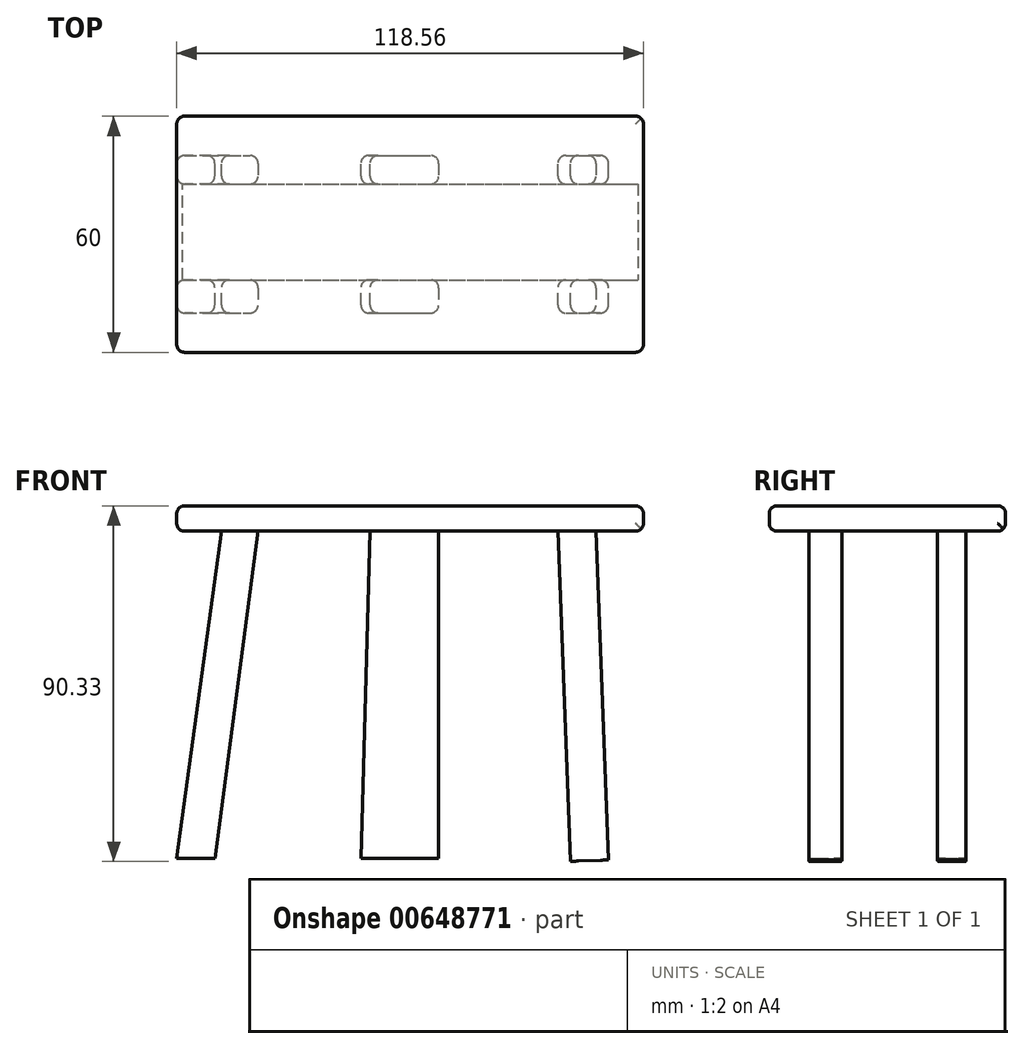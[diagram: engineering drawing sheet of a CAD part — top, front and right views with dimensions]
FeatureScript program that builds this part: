
annotation { "Feature Type Name" : "Feature", "Feature Type Description" : "" }
export const myFeature = defineFeature(function(context is Context, id is Id, definition is map)
    precondition{}
    {
        {
            var Q0;
            Q0=qCreatedBy(makeId("Front.planeOp"),FACE);
            var sketch = newSketch(context, id + "F0", { "sketchPlane" : qUnion([Q0])});
            skLineSegment(sketch, "E0.bottom", {"start": v(-56.26, 27.02) * mm, "end": v(62.3, 27.02) * mm});
            skLineSegment(sketch, "E0.top", {"start": v(-56.26, 20.57) * mm, "end": v(62.3, 20.57) * mm});
            skLineSegment(sketch, "E0.left", {"start": v(-56.26, 27.02) * mm, "end": v(-56.26, 20.57) * mm});
            skLineSegment(sketch, "E0.right", {"start": v(62.3, 27.02) * mm, "end": v(62.3, 20.57) * mm});
            skSolve(sketch);
        }
        {
            var Q0;
            Q0=makeQuery(id+"F0.imprint","IMPRINT",FACE,{"disambiguationData":[TD([[makeQuery(id+"F0.imprint","IMPRINT",EDGE,{"derivedFrom":sQuery(id+"F0.wireOp",EDGE,"E0.bottom")}),-1.0]])]});
            extrude(context, id + "F1", {"entities" : qUnion([Q0]), "depth" : 60 * mm, "offsetDistance" : 25 * mm});
        }
        {
            var Q0;
            Q0=qCreatedBy(makeId("Front.planeOp"),FACE);
            cPlane(context, id + "F2", {"entities" : qUnion([Q0]), "cplaneType" : CPlaneType.OFFSET, "offset" : 10 * mm, "width" : 150 * mm, "height" : 150 * mm});
        }
        {
            var Q0;
            Q0=qCreatedBy(id+"F2.planeOp",FACE);
            var sketch = newSketch(context, id + "F3", { "sketchPlane" : qUnion([Q0])});
            skLineSegment(sketch, "E1", {"start": v(-44.56, 22.99) * mm, "end": v(-56.26, -62.5) * mm});
            skLineSegment(sketch, "E2", {"start": v(-56.26, -62.5) * mm, "end": v(-46.58, -62.5) * mm});
            skLineSegment(sketch, "E3", {"start": v(-46.58, -62.5) * mm, "end": v(-35.29, 22.99) * mm});
            skLineSegment(sketch, "E4", {"start": v(-35.29, 22.99) * mm, "end": v(-44.56, 22.99) * mm});
            skLineSegment(sketch, "E5", {"start": v(-7.06, 22.99) * mm, "end": v(-9.48, -62.5) * mm});
            skPoint(sketch, "E5.startSnap0", {"position": v(-39.92, 22.99) * mm});
            skLineSegment(sketch, "E6", {"start": v(-9.48, -62.5) * mm, "end": v(10.28, -62.5) * mm});
            skLineSegment(sketch, "E7", {"start": v(10.28, -62.5) * mm, "end": v(10.28, 22.99) * mm});
            skLineSegment(sketch, "E8", {"start": v(10.28, 22.99) * mm, "end": v(-7.06, 22.99) * mm});
            skLineSegment(sketch, "E9", {"start": v(40.53, 22.18) * mm, "end": v(43.75, -63.31) * mm});
            skLineSegment(sketch, "E10", {"start": v(43.75, -63.31) * mm, "end": v(53.42, -62.95) * mm});
            skLineSegment(sketch, "E11", {"start": v(53.42, -62.95) * mm, "end": v(50.2, 22.27) * mm});
            skLineSegment(sketch, "E12", {"start": v(50.2, 22.27) * mm, "end": v(40.53, 22.18) * mm});
            skSolve(sketch);
        }
        {
            var Q0;
            Q0 = qSketchRegion(id + "F3", true);
            extrude(context, id + "F4", {"entities" : qUnion([Q0]), "operationType" : NewBodyOperationType.ADD, "depth" : 40 * mm, "offsetDistance" : 25 * mm});
        }
        {
            var Q0;
            Q0=qCreatedBy(makeId("Right.planeOp"),FACE);
            var sketch = newSketch(context, id + "F5", { "sketchPlane" : qUnion([Q0])});
            skLineSegment(sketch, "E13.bottom", {"start": v(-41.6, 20.65) * mm, "end": v(-17.23, 20.65) * mm});
            skLineSegment(sketch, "E13.top", {"start": v(-41.6, -66.54) * mm, "end": v(-17.23, -66.54) * mm});
            skLineSegment(sketch, "E13.left", {"start": v(-41.6, 20.65) * mm, "end": v(-41.6, -66.54) * mm});
            skLineSegment(sketch, "E13.right", {"start": v(-17.23, 20.65) * mm, "end": v(-17.23, -66.54) * mm});
            skSolve(sketch);
        }
        {
            var Q0;
            Q0 = qSketchRegion(id + "F5", true);
            extrude(context, id + "F6", {"entities" : qUnion([Q0]), "operationType" : NewBodyOperationType.REMOVE, "endBound" : BoundingType.THROUGH_ALL, "oppositeDirection" : true, "depth" : 100 * mm, "offsetDistance" : 25 * mm, "hasSecondDirection" : true, "secondDirectionOppositeDirection" : false, "secondDirectionDepth" : 100 * mm});
        }
        {
            var Q0;
            Q0=makeQuery(id+"F1.opExtrude","SWEPT_EDGE",EDGE,{"disambiguationData":[OSD([sQuery(id+"F0.wireOp",EDGE,"E0.bottom"),sQuery(id+"F0.wireOp",EDGE,"E0.left")])]});
            var Q1;
            Q1=makeQuery(id+"F1.opExtrude","CAP_EDGE",EDGE,{"disambiguationData":[OSD([sQuery(id+"F0.wireOp",EDGE,"E0.bottom")])],"isStart":false});
            var Q2;
            Q2=makeQuery(id+"F1.opExtrude","SWEPT_EDGE",EDGE,{"disambiguationData":[OSD([sQuery(id+"F0.wireOp",EDGE,"E0.bottom"),sQuery(id+"F0.wireOp",EDGE,"E0.right")])]});
            var Q3;
            Q3=makeQuery(id+"F1.opExtrude","CAP_EDGE",EDGE,{"disambiguationData":[OSD([sQuery(id+"F0.wireOp",EDGE,"E0.bottom")])],"isStart":true});
            var Q4;
            Q4=makeQuery(id+"F1.opExtrude","CAP_EDGE",EDGE,{"disambiguationData":[OSD([sQuery(id+"F0.wireOp",EDGE,"E0.left")])],"isStart":false});
            var Q5;
            Q5=makeQuery(id+"F1.opExtrude","CAP_EDGE",EDGE,{"disambiguationData":[OSD([sQuery(id+"F0.wireOp",EDGE,"E0.left")])],"isStart":true});
            var Q6;
            {var subQ0=sQuery(id+"F0.wireOp",EDGE,"E0.left");var subQ1=sQuery(id+"F0.wireOp",EDGE,"E0.top");Q6=makeQuery(id+"F6.boolean.opBoolean","SPLIT",EDGE,{"disambiguationData":[TD([makeQuery(id+"F6.opExtrude","SWEPT_FACE",FACE,{"disambiguationData":[OSD([sQuery(id+"F5.wireOp",EDGE,"E13.right")])]})])],"derivedFrom":makeQuery(id+"F1.opExtrude","SWEPT_EDGE",EDGE,{"disambiguationData":[OSD([subQ1,subQ0])]})});}
            var Q7;
            {var subQ0=sQuery(id+"F0.wireOp",EDGE,"E0.left");var subQ1=sQuery(id+"F0.wireOp",EDGE,"E0.top");Q7=makeQuery(id+"F6.boolean.opBoolean","SPLIT",EDGE,{"disambiguationData":[TD([makeQuery(id+"F6.opExtrude","SWEPT_FACE",FACE,{"disambiguationData":[OSD([sQuery(id+"F5.wireOp",EDGE,"E13.left")])]})])],"derivedFrom":makeQuery(id+"F1.opExtrude","SWEPT_EDGE",EDGE,{"disambiguationData":[OSD([subQ1,subQ0])]})});}
            var Q8;
            {var subQ0=sQuery(id+"F0.wireOp",EDGE,"E0.right");var subQ1=sQuery(id+"F0.wireOp",EDGE,"E0.top");Q8=makeQuery(id+"F6.boolean.opBoolean","SPLIT",EDGE,{"disambiguationData":[TD([makeQuery(id+"F6.opExtrude","SWEPT_FACE",FACE,{"disambiguationData":[OSD([sQuery(id+"F5.wireOp",EDGE,"E13.left")])]})])],"derivedFrom":makeQuery(id+"F1.opExtrude","SWEPT_EDGE",EDGE,{"disambiguationData":[OSD([subQ1,subQ0])]})});}
            var Q9;
            Q9=makeQuery(id+"F1.opExtrude","CAP_EDGE",EDGE,{"disambiguationData":[OSD([sQuery(id+"F0.wireOp",EDGE,"E0.top")])],"isStart":false});
            var Q10;
            Q10=makeQuery(id+"F1.opExtrude","CAP_EDGE",EDGE,{"disambiguationData":[OSD([sQuery(id+"F0.wireOp",EDGE,"E0.right")])],"isStart":false});
            var Q11;
            Q11=makeQuery(id+"F1.opExtrude","CAP_EDGE",EDGE,{"disambiguationData":[OSD([sQuery(id+"F0.wireOp",EDGE,"E0.right")])],"isStart":true});
            var Q12;
            Q12=makeQuery(id+"F1.opExtrude","CAP_EDGE",EDGE,{"disambiguationData":[OSD([sQuery(id+"F0.wireOp",EDGE,"E0.top")])],"isStart":true});
            var Q13;
            Q13=makeQuery(id+"F4.opExtrude","CAP_EDGE",EDGE,{"disambiguationData":[OSD([sQuery(id+"F3.wireOp",EDGE,"E11")])],"isStart":true});
            var Q14;
            Q14=makeQuery(id+"F4.opExtrude","CAP_EDGE",EDGE,{"disambiguationData":[OSD([sQuery(id+"F3.wireOp",EDGE,"E9")])],"isStart":true});
            var Q15;
            Q15=makeQuery(id+"F4.opExtrude","CAP_EDGE",EDGE,{"disambiguationData":[OSD([sQuery(id+"F3.wireOp",EDGE,"E7")])],"isStart":true});
            var Q16;
            Q16=makeQuery(id+"F6.boolean.opBoolean","INTERSECT",EDGE,{"derivedFrom":[makeQuery(id+"F4.opExtrude","SWEPT_FACE",FACE,{"disambiguationData":[OSD([sQuery(id+"F3.wireOp",EDGE,"E7")])]}),makeQuery(id+"F6.opExtrude","SWEPT_FACE",FACE,{"disambiguationData":[OSD([sQuery(id+"F5.wireOp",EDGE,"E13.right")])]})]});
            var Q17;
            Q17=makeQuery(id+"F4.opExtrude","CAP_EDGE",EDGE,{"disambiguationData":[OSD([sQuery(id+"F3.wireOp",EDGE,"E5")])],"isStart":true});
            var Q18;
            Q18=makeQuery(id+"F4.opExtrude","CAP_EDGE",EDGE,{"disambiguationData":[OSD([sQuery(id+"F3.wireOp",EDGE,"E3")])],"isStart":true});
            var Q19;
            Q19=makeQuery(id+"F4.opExtrude","CAP_EDGE",EDGE,{"disambiguationData":[OSD([sQuery(id+"F3.wireOp",EDGE,"E1")])],"isStart":true});
            var Q20;
            Q20=makeQuery(id+"F6.boolean.opBoolean","INTERSECT",EDGE,{"derivedFrom":[makeQuery(id+"F4.opExtrude","SWEPT_FACE",FACE,{"disambiguationData":[OSD([sQuery(id+"F3.wireOp",EDGE,"E3")])]}),makeQuery(id+"F6.opExtrude","SWEPT_FACE",FACE,{"disambiguationData":[OSD([sQuery(id+"F5.wireOp",EDGE,"E13.right")])]})]});
            var Q21;
            Q21=makeQuery(id+"F6.boolean.opBoolean","INTERSECT",EDGE,{"derivedFrom":[makeQuery(id+"F4.opExtrude","SWEPT_FACE",FACE,{"disambiguationData":[OSD([sQuery(id+"F3.wireOp",EDGE,"E3")])]}),makeQuery(id+"F6.opExtrude","SWEPT_FACE",FACE,{"disambiguationData":[OSD([sQuery(id+"F5.wireOp",EDGE,"E13.left")])]})]});
            var Q22;
            Q22=makeQuery(id+"F6.boolean.opBoolean","INTERSECT",EDGE,{"derivedFrom":[makeQuery(id+"F4.opExtrude","SWEPT_FACE",FACE,{"disambiguationData":[OSD([sQuery(id+"F3.wireOp",EDGE,"E5")])]}),makeQuery(id+"F6.opExtrude","SWEPT_FACE",FACE,{"disambiguationData":[OSD([sQuery(id+"F5.wireOp",EDGE,"E13.right")])]})]});
            var Q23;
            Q23=makeQuery(id+"F6.boolean.opBoolean","INTERSECT",EDGE,{"derivedFrom":[makeQuery(id+"F4.opExtrude","SWEPT_FACE",FACE,{"disambiguationData":[OSD([sQuery(id+"F3.wireOp",EDGE,"E1")])]}),makeQuery(id+"F6.opExtrude","SWEPT_FACE",FACE,{"disambiguationData":[OSD([sQuery(id+"F5.wireOp",EDGE,"E13.right")])]})]});
            var Q24;
            Q24=makeQuery(id+"F4.opExtrude","CAP_EDGE",EDGE,{"disambiguationData":[OSD([sQuery(id+"F3.wireOp",EDGE,"E1")])],"isStart":false});
            var Q25;
            Q25=makeQuery(id+"F6.boolean.opBoolean","INTERSECT",EDGE,{"derivedFrom":[makeQuery(id+"F4.opExtrude","SWEPT_FACE",FACE,{"disambiguationData":[OSD([sQuery(id+"F3.wireOp",EDGE,"E1")])]}),makeQuery(id+"F6.opExtrude","SWEPT_FACE",FACE,{"disambiguationData":[OSD([sQuery(id+"F5.wireOp",EDGE,"E13.left")])]})]});
            var Q26;
            Q26=makeQuery(id+"F4.opExtrude","CAP_EDGE",EDGE,{"disambiguationData":[OSD([sQuery(id+"F3.wireOp",EDGE,"E3")])],"isStart":false});
            var Q27;
            Q27=makeQuery(id+"F4.opExtrude","CAP_EDGE",EDGE,{"disambiguationData":[OSD([sQuery(id+"F3.wireOp",EDGE,"E5")])],"isStart":false});
            var Q28;
            Q28=makeQuery(id+"F6.boolean.opBoolean","INTERSECT",EDGE,{"derivedFrom":[makeQuery(id+"F4.opExtrude","SWEPT_FACE",FACE,{"disambiguationData":[OSD([sQuery(id+"F3.wireOp",EDGE,"E5")])]}),makeQuery(id+"F6.opExtrude","SWEPT_FACE",FACE,{"disambiguationData":[OSD([sQuery(id+"F5.wireOp",EDGE,"E13.left")])]})]});
            var Q29;
            Q29=makeQuery(id+"F4.opExtrude","CAP_EDGE",EDGE,{"disambiguationData":[OSD([sQuery(id+"F3.wireOp",EDGE,"E7")])],"isStart":false});
            var Q30;
            Q30=makeQuery(id+"F6.boolean.opBoolean","INTERSECT",EDGE,{"derivedFrom":[makeQuery(id+"F4.opExtrude","SWEPT_FACE",FACE,{"disambiguationData":[OSD([sQuery(id+"F3.wireOp",EDGE,"E7")])]}),makeQuery(id+"F6.opExtrude","SWEPT_FACE",FACE,{"disambiguationData":[OSD([sQuery(id+"F5.wireOp",EDGE,"E13.left")])]})]});
            var Q31;
            Q31=makeQuery(id+"F6.boolean.opBoolean","INTERSECT",EDGE,{"derivedFrom":[makeQuery(id+"F4.opExtrude","SWEPT_FACE",FACE,{"disambiguationData":[OSD([sQuery(id+"F3.wireOp",EDGE,"E9")])]}),makeQuery(id+"F6.opExtrude","SWEPT_FACE",FACE,{"disambiguationData":[OSD([sQuery(id+"F5.wireOp",EDGE,"E13.left")])]})]});
            var Q32;
            Q32=makeQuery(id+"F6.boolean.opBoolean","INTERSECT",EDGE,{"derivedFrom":[makeQuery(id+"F4.opExtrude","SWEPT_FACE",FACE,{"disambiguationData":[OSD([sQuery(id+"F3.wireOp",EDGE,"E9")])]}),makeQuery(id+"F6.opExtrude","SWEPT_FACE",FACE,{"disambiguationData":[OSD([sQuery(id+"F5.wireOp",EDGE,"E13.right")])]})]});
            var Q33;
            Q33=makeQuery(id+"F4.opExtrude","CAP_EDGE",EDGE,{"disambiguationData":[OSD([sQuery(id+"F3.wireOp",EDGE,"E9")])],"isStart":false});
            var Q34;
            Q34=makeQuery(id+"F6.boolean.opBoolean","INTERSECT",EDGE,{"derivedFrom":[makeQuery(id+"F4.opExtrude","SWEPT_FACE",FACE,{"disambiguationData":[OSD([sQuery(id+"F3.wireOp",EDGE,"E11")])]}),makeQuery(id+"F6.opExtrude","SWEPT_FACE",FACE,{"disambiguationData":[OSD([sQuery(id+"F5.wireOp",EDGE,"E13.right")])]})]});
            var Q35;
            Q35=makeQuery(id+"F6.boolean.opBoolean","INTERSECT",EDGE,{"derivedFrom":[makeQuery(id+"F4.opExtrude","SWEPT_FACE",FACE,{"disambiguationData":[OSD([sQuery(id+"F3.wireOp",EDGE,"E11")])]}),makeQuery(id+"F6.opExtrude","SWEPT_FACE",FACE,{"disambiguationData":[OSD([sQuery(id+"F5.wireOp",EDGE,"E13.left")])]})]});
            var Q36;
            Q36=makeQuery(id+"F4.opExtrude","CAP_EDGE",EDGE,{"disambiguationData":[OSD([sQuery(id+"F3.wireOp",EDGE,"E11")])],"isStart":false});
            fillet(context, id + "F7", {"entities" : qUnion([Q0, Q1, Q2, Q3, Q4, Q5, Q6, Q7, Q8, Q9, Q10, Q11, Q12, Q13, Q14, Q15, Q16, Q17, Q18, Q19, Q20, Q21, Q22, Q23, Q24, Q25, Q26, Q27, Q28, Q29, Q30, Q31, Q32, Q33, Q34, Q35, Q36]), "radius" : 2 * mm, "tangentPropagation" : true, "allowEdgeOverflow" : false});
        }
    });
